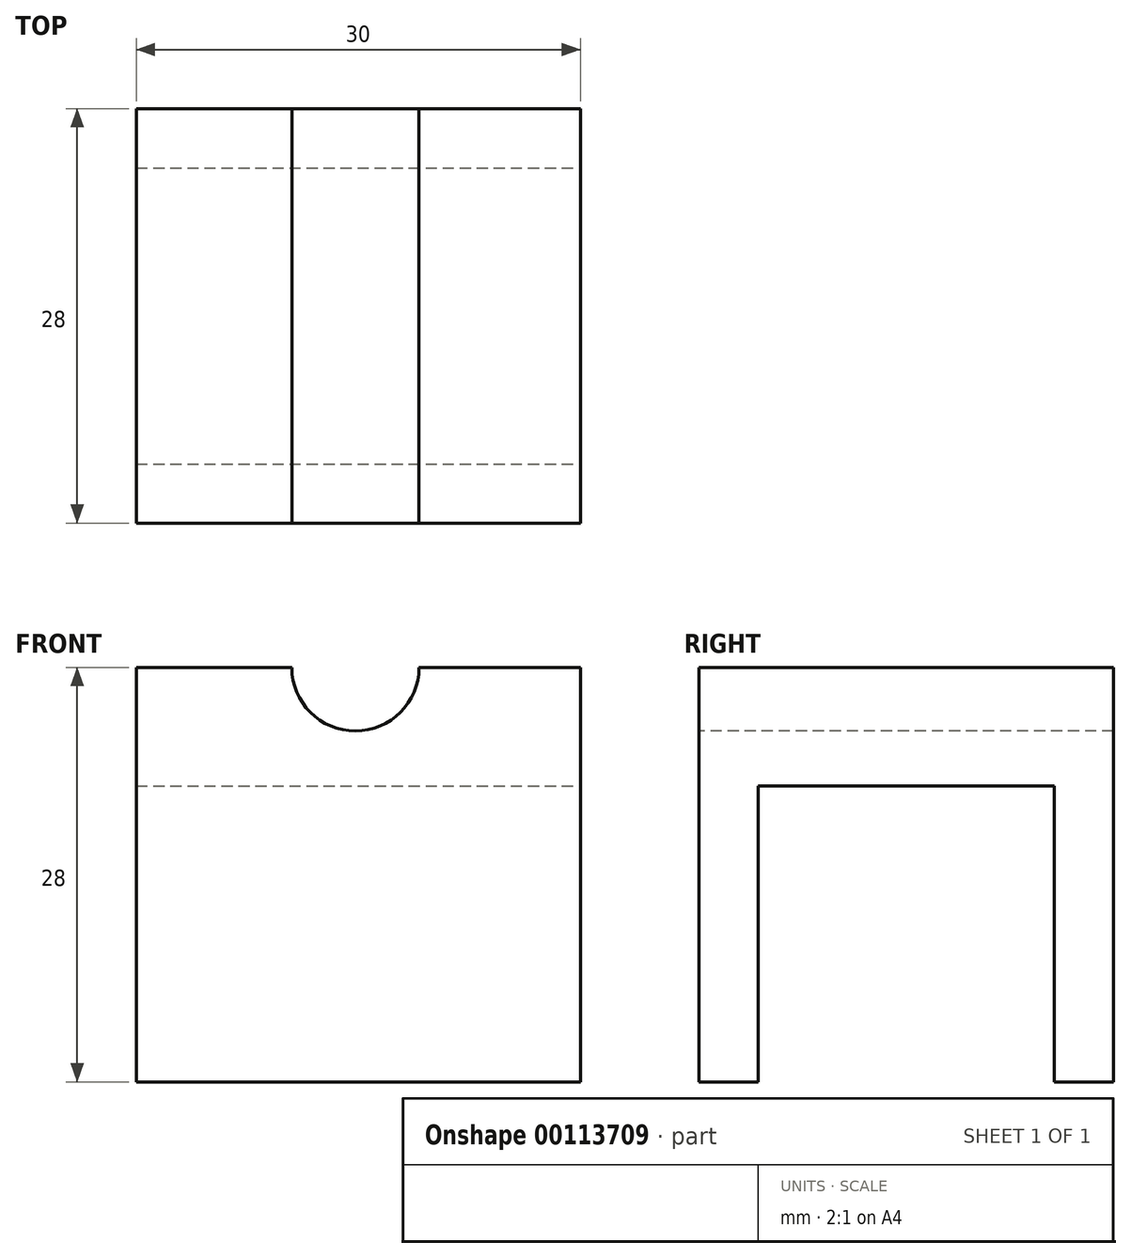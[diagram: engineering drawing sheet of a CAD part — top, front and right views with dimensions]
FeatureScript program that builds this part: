
annotation { "Feature Type Name" : "Feature", "Feature Type Description" : "" }
export const myFeature = defineFeature(function(context is Context, id is Id, definition is map)
    precondition{}
    {
        {
            var Q0;
            Q0=qCreatedBy(makeId("Top.planeOp"),FACE);
            var sketch = newSketch(context, id + "F0", { "sketchPlane" : qUnion([Q0])});
            skLineSegment(sketch, "E0.bottom", {"start": v(-14.8, 14.45) * mm, "end": v(15.2, 14.45) * mm});
            skLineSegment(sketch, "E0.top", {"start": v(-14.8, -13.55) * mm, "end": v(15.2, -13.55) * mm});
            skLineSegment(sketch, "E0.left", {"start": v(-14.8, 14.45) * mm, "end": v(-14.8, -13.55) * mm});
            skLineSegment(sketch, "E0.right", {"start": v(15.2, 14.45) * mm, "end": v(15.2, -13.55) * mm});
            skSolve(sketch);
        }
        {
            var Q0;
            Q0=makeQuery(id+"F0.imprint","IMPRINT",FACE,{"disambiguationData":[TD([[makeQuery(id+"F0.imprint","IMPRINT",EDGE,{"derivedFrom":sQuery(id+"F0.wireOp",EDGE,"E0.bottom")}),-1.0]])]});
            extrude(context, id + "F1", {"entities" : qUnion([Q0]), "depth" : 28 * mm});
        }
        {
            var Q0;
            Q0=makeQuery(id+"F1.opExtrude","SWEPT_FACE",FACE,{"disambiguationData":[OSD([sQuery(id+"F0.wireOp",EDGE,"E0.top")])]});
            var sketch = newSketch(context, id + "F2", { "sketchPlane" : qUnion([Q0])});
            skCircle(sketch, "E1", {"center": v(0, 28) * mm, "radius": 4.3 * mm});
            skSolve(sketch);
        }
        {
            var Q0;
            {var subQ0=sQuery(id+"F2.wireOp",EDGE,"E1");var subQ1=makeQuery(id+"F1.opExtrude","CAP_EDGE",EDGE,{"disambiguationData":[OSD([sQuery(id+"F0.wireOp",EDGE,"E0.top")])],"isStart":false});var subQ2=makeQuery(id+"F2.imprint","INTERSECT",VERTEX,{"disambiguationData":[OD(0.0)],"derivedFrom":[subQ1,subQ0]});Q0=makeQuery(id+"F2.imprint","IMPRINT",FACE,{"disambiguationData":[TD([[makeQuery(id+"F2.imprint","IMPRINT",EDGE,{"disambiguationData":[TD([[subQ2,-1.0]])],"derivedFrom":subQ0}),1.0]])]});}
            extrude(context, id + "F3", {"entities" : qUnion([Q0]), "operationType" : NewBodyOperationType.REMOVE, "endBound" : BoundingType.THROUGH_ALL, "oppositeDirection" : true, "depth" : 25 * mm});
        }
        {
            var Q0;
            Q0=makeQuery(id+"F1.opExtrude","CAP_FACE",FACE,{"disambiguationData":[OSD([sQuery(id+"F0.wireOp",EDGE,"E0.bottom"),sQuery(id+"F0.wireOp",EDGE,"E0.top"),sQuery(id+"F0.wireOp",EDGE,"E0.left"),sQuery(id+"F0.wireOp",EDGE,"E0.right")])],"isStart":true});
            var sketch = newSketch(context, id + "F4", { "sketchPlane" : qUnion([Q0])});
            skLineSegment(sketch, "E2.bottom", {"start": v(-14.8, 9.55) * mm, "end": v(15.2, 9.55) * mm});
            skLineSegment(sketch, "E2.top", {"start": v(-14.8, -10.45) * mm, "end": v(15.2, -10.45) * mm});
            skLineSegment(sketch, "E2.left", {"start": v(-14.8, 9.55) * mm, "end": v(-14.8, -10.45) * mm});
            skLineSegment(sketch, "E2.right", {"start": v(15.2, 9.55) * mm, "end": v(15.2, -10.45) * mm});
            skSolve(sketch);
        }
        {
            var Q0;
            Q0=makeQuery(id+"F4.imprint","IMPRINT",FACE,{"disambiguationData":[TD([[makeQuery(id+"F4.imprint","IMPRINT",EDGE,{"derivedFrom":sQuery(id+"F4.wireOp",EDGE,"E2.bottom")}),-1.0]])]});
            extrude(context, id + "F5", {"entities" : qUnion([Q0]), "operationType" : NewBodyOperationType.REMOVE, "oppositeDirection" : true, "depth" : 20 * mm});
        }
    });
